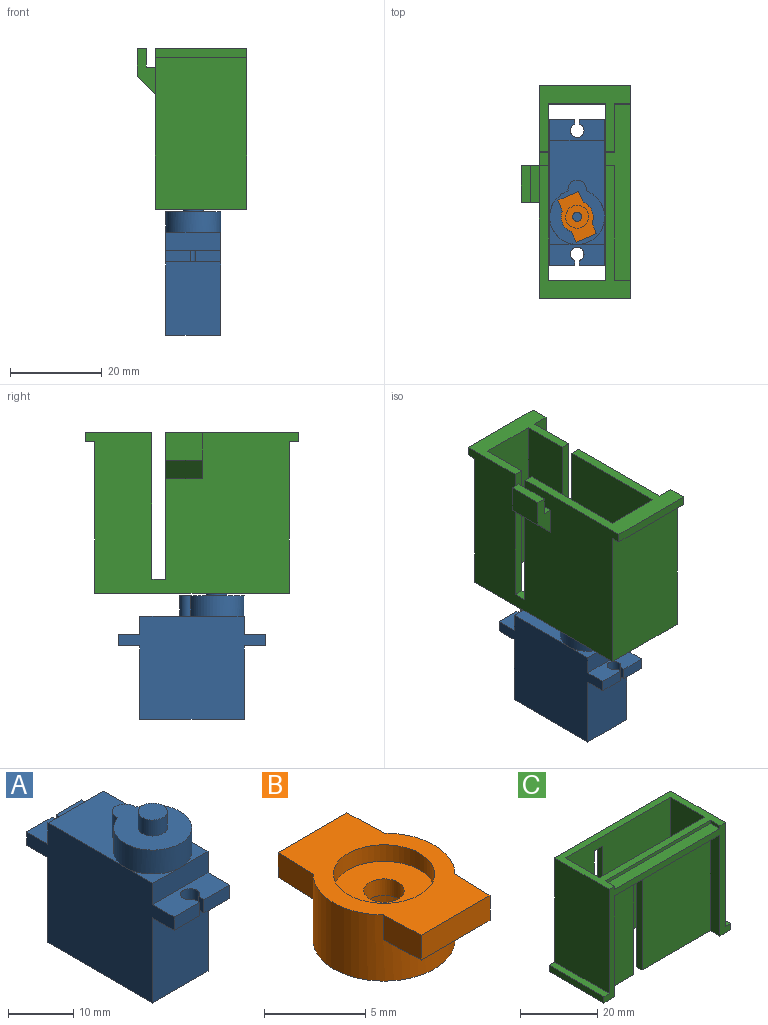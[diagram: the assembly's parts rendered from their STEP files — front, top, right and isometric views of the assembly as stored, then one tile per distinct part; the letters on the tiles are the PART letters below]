
ASSEMBLY  parts=3 mates=2
PART A: 29 faces, bbox 12x32x30 mm
  f0: plane 12x4.63mm, normal (0,0,-1), area 47.4mm2, adj f2,f8,f9,f10,f13,f26,f27,f28
  f1: plane 5.5x2.5mm, normal (0,1,0), area 13.7mm2, adj f6,f10,f14,f25
  f2: plane 5.5x2.5mm, normal (0,-1,0), area 13.7mm2, adj f0,f3,f10,f26
  f3: plane 12x4.63mm, normal (0,0,1), area 47.4mm2, adj f2,f8,f10,f13,f16,f26,f27,f28
  f4: plane 16.75x12mm, normal (0,0,1), area 137.7mm2, adj f8,f10,f15,f18,f19
  f5: plane 6x6mm, normal (0,0,1), area 7.7mm2, adj f8,f16,f19
  f6: plane 12x4.63mm, normal (0,0,1), area 47.4mm2, adj f1,f8,f10,f12,f15,f23,f24,f25
  f7: plane 16x12mm, normal (0,1,0), area 192mm2, adj f8,f10,f11,f14
  f8: plane 32x22.5mm, normal (-1,0,0), area 535mm2, adj f0,f3,f4,f5,f6,f7,f9,f11
  f9: plane 16x12mm, normal (0,-1,0), area 192mm2, adj f0,f8,f10,f11
  f10: plane 32x22.5mm, normal (1,0,0), area 535mm2, adj f0,f1,f2,f3,f4,f6,f7,f9
  f11: plane 22.75x12mm, normal (0,0,-1), area 273mm2, adj f7,f8,f9,f10
  f12: plane 5.5x2.5mm, normal (0,1,0), area 13.7mm2, adj f6,f8,f14,f24
  f13: plane 5.5x2.5mm, normal (0,-1,0), area 13.7mm2, adj f0,f3,f8,f27
  f14: plane 12x4.63mm, normal (0,0,-1), area 47.4mm2, adj f1,f7,f8,f10,f12,f23,f24,f25
  f15: plane 12x4mm, normal (0,1,0), area 48mm2, adj f4,f6,f8,f10
  f16: plane 12x4mm, normal (0,-1,0), area 48mm2, adj f3,f5,f8,f10,f17
  f17: plane 6x6mm, normal (0,0,1), area 7.7mm2, adj f10,f16,f19
  f18: cylinder r=2mm len=4.5mm, axis (0,0,-1), area 31.3mm2, adj f4,f19,f20
  f19: cylinder r=6mm len=12mm, axis (0,0,-1), area 151.6mm2, adj f4,f5,f17,f18,f20
  f20: plane 14x12mm, normal (0,0,1), area 103.9mm2, adj f18,f19,f21
  f21: cylinder r=2.25mm len=4.5mm, axis (0,0,-1), area 42.4mm2, adj f20,f22
  f22: plane 4.5x4.5mm, normal (0,0,1), area 15.9mm2, adj f21
  f23: cylinder r=1.5mm len=3mm, axis (0,0,1), area 21mm2, adj f6,f14,f24,f25
  f24: plane 2.5x1.09mm, normal (1,0,0), area 2.7mm2, adj f6,f12,f14,f23
  f25: plane 2.5x1.09mm, normal (-1,0,0), area 2.7mm2, adj f1,f6,f14,f23
  f26: plane 2.5x1.09mm, normal (-1,0,0), area 2.7mm2, adj f0,f2,f3,f28
  f27: plane 2.5x1.09mm, normal (1,0,0), area 2.7mm2, adj f0,f3,f13,f28
  f28: cylinder r=1.5mm len=3mm, axis (0,0,1), area 21mm2, adj f0,f3,f26,f27
PART B: 16 faces, bbox 7x10x4 mm
  f0: cylinder r=2.5mm len=5mm, axis (0,0,1), area 31.4mm2, adj f3,f7
  f1: cylinder r=2.5mm len=5mm, axis (0,0,1), area 15.7mm2, adj f4,f6
  f2: cylinder r=3.5mm len=7mm, axis (0,0,1), area 71.3mm2, adj f3,f4,f8,f9,f11,f12,f13,f15
  f3: plane 7x7mm, normal (0,0,-1), area 18.8mm2, adj f0,f2
  f4: plane 10x7mm, normal (0,0,1), area 36.6mm2, adj f1,f2,f8,f9,f10,f12,f13,f14
  f5: cylinder r=1mm len=2mm, axis (0,0,-1), area 6.3mm2, adj f6,f7
  f6: plane 5x5mm, normal (0,0,1), area 16.5mm2, adj f1,f5
  f7: plane 5x5mm, normal (0,0,-1), area 16.5mm2, adj f0,f5
  f8: plane 2.55x1.5mm, normal (-1,0.04,0), area 3.8mm2, adj f2,f4,f10,f11
  f9: plane 2.55x1.5mm, normal (1,0.04,0), area 3.8mm2, adj f2,f4,f10,f11
  f10: plane 4.8x1.5mm, normal (0,1,0), area 7.2mm2, adj f4,f8,f9,f11
  f11: plane 5x2.55mm, normal (0,0,-1), area 8.9mm2, adj f2,f8,f9,f10
  f12: plane 2.55x1.5mm, normal (1,-0.04,0), area 3.8mm2, adj f2,f4,f14,f15
  f13: plane 2.55x1.5mm, normal (-1,-0.04,0), area 3.8mm2, adj f2,f4,f14,f15
  f14: plane 4.8x1.5mm, normal (0,-1,0), area 7.2mm2, adj f4,f12,f13,f15
  f15: plane 5x2.55mm, normal (0,0,-1), area 8.9mm2, adj f2,f12,f13,f14
PART C: 35 faces, bbox 46.5x24x35 mm
  f0: plane 29x20mm, normal (0,0,-1), area 180mm2, adj f1,f6,f7,f9,f13,f14,f18,f21
  f1: plane 32x25mm, normal (0,-1,0), area 800mm2, adj f0,f6,f31,f33
  f2: plane 3.5x1mm, normal (-1,0,0), area 3.5mm2, adj f4,f14,f15,f32
  f3: plane 32x3.5mm, normal (1,0,0), area 112mm2, adj f8,f14,f29,f31
  f4: plane 38.5x1mm, normal (0,-1,0), area 38.5mm2, adj f2,f12,f15,f32
  f5: plane 35x12.5mm, normal (1,0,0), area 437.5mm2, adj f7,f8,f15,f30
  f6: plane 32x3.5mm, normal (-1,0,0), area 112mm2, adj f0,f1,f14,f31
  f7: plane 38.5x35mm, normal (0,-1,0), area 1251.5mm2, adj f0,f5,f8,f13,f15,f21,f27,f28
  f8: plane 20x14.5mm, normal (0,0,-1), area 122mm2, adj f3,f5,f7,f9,f14,f20,f27,f29
  f9: plane 46.5x35mm, normal (0,1,0), area 1351.5mm2, adj f0,f8,f10,f11,f15,f17,f18,f19
  f10: plane 33x20mm, normal (1,0,0), area 660mm2, adj f9,f14,f15,f17
  f11: plane 33x20mm, normal (-1,0,0), area 660mm2, adj f9,f14,f15,f19
  f12: plane 3.5x1mm, normal (1,0,0), area 3.5mm2, adj f4,f14,f15,f32
  f13: plane 35x12.5mm, normal (-1,0,0), area 437.5mm2, adj f0,f7,f15,f30
  f14: plane 46.5x35mm, normal (0,-1,0), area 225mm2, adj f0,f2,f3,f6,f8,f10,f11,f12
  f15: plane 42.5x20mm, normal (0,0,1), area 234mm2, adj f2,f4,f5,f7,f9,f10,f11,f12
  f16: plane 8x2mm, normal (0,0,-1), area 16mm2, adj f21,f22,f23,f25
  f17: plane 20x2mm, normal (0,0,1), area 40mm2, adj f9,f10,f14,f18
  f18: plane 20x2mm, normal (1,0,0), area 40mm2, adj f0,f9,f14,f17
  f19: plane 20x2mm, normal (0,0,1), area 40mm2, adj f9,f11,f14,f20
  f20: plane 20x2mm, normal (-1,0,0), area 40mm2, adj f8,f9,f14,f19
  f21: plane 32x6mm, normal (-1,0,0), area 88mm2, adj f0,f7,f9,f16,f23,f24,f25,f26
  f22: plane 10x4mm, normal (1,0,0), area 24mm2, adj f9,f16,f23,f24,f25,f26
  f23: plane 8x6mm, normal (0,1,0), area 48mm2, adj f16,f21,f22,f26
  f24: plane 8x2mm, normal (0,0,-1), area 16mm2, adj f9,f21,f22,f25
  f25: plane 8x4mm, normal (0,-1,0), area 32mm2, adj f16,f21,f22,f24
  f26: plane 8x4mm, normal (0,0.71,0.71), area 45.3mm2, adj f9,f21,f22,f23
  f27: plane 32x2mm, normal (1,0,0), area 64mm2, adj f7,f8,f9,f28
  f28: plane 3x2mm, normal (0,0,-1), area 6mm2, adj f7,f9,f21,f27
  f29: plane 32x10.5mm, normal (0,-1,0), area 336mm2, adj f3,f8,f31,f34
  f30: plane 38.5x35mm, normal (0,1,0), area 1251.5mm2, adj f0,f5,f8,f13,f15,f31,f33,f34
  f31: plane 38.5x5.5mm, normal (0,0,-1), area 140.8mm2, adj f1,f3,f6,f14,f29,f30,f33,f34
  f32: plane 38.5x3.5mm, normal (0,0,1), area 134.8mm2, adj f2,f4,f12,f14
  f33: plane 32x2mm, normal (-1,0,0), area 64mm2, adj f0,f1,f30,f31
  f34: plane 32x2mm, normal (1,0,0), area 64mm2, adj f8,f29,f30,f31
PLACE A t=(8.25,23.25,-62.55)mm
PLACE B rot(axis=(0,0,1),23.3deg) t=(6.12,22.81,-62.55)mm
PLACE C rot(axis=(0.71,-0.71,0),180deg) t=(0,23.25,0)mm
MATE revolute A.f21 <-> B.f0  axis (0,0,1) through (8.25,17.88,-32.55)mm
MATE slider A.f11 <-> C.f15  axis (0,0,-1) through (8.25,23.25,-62.55)mm
